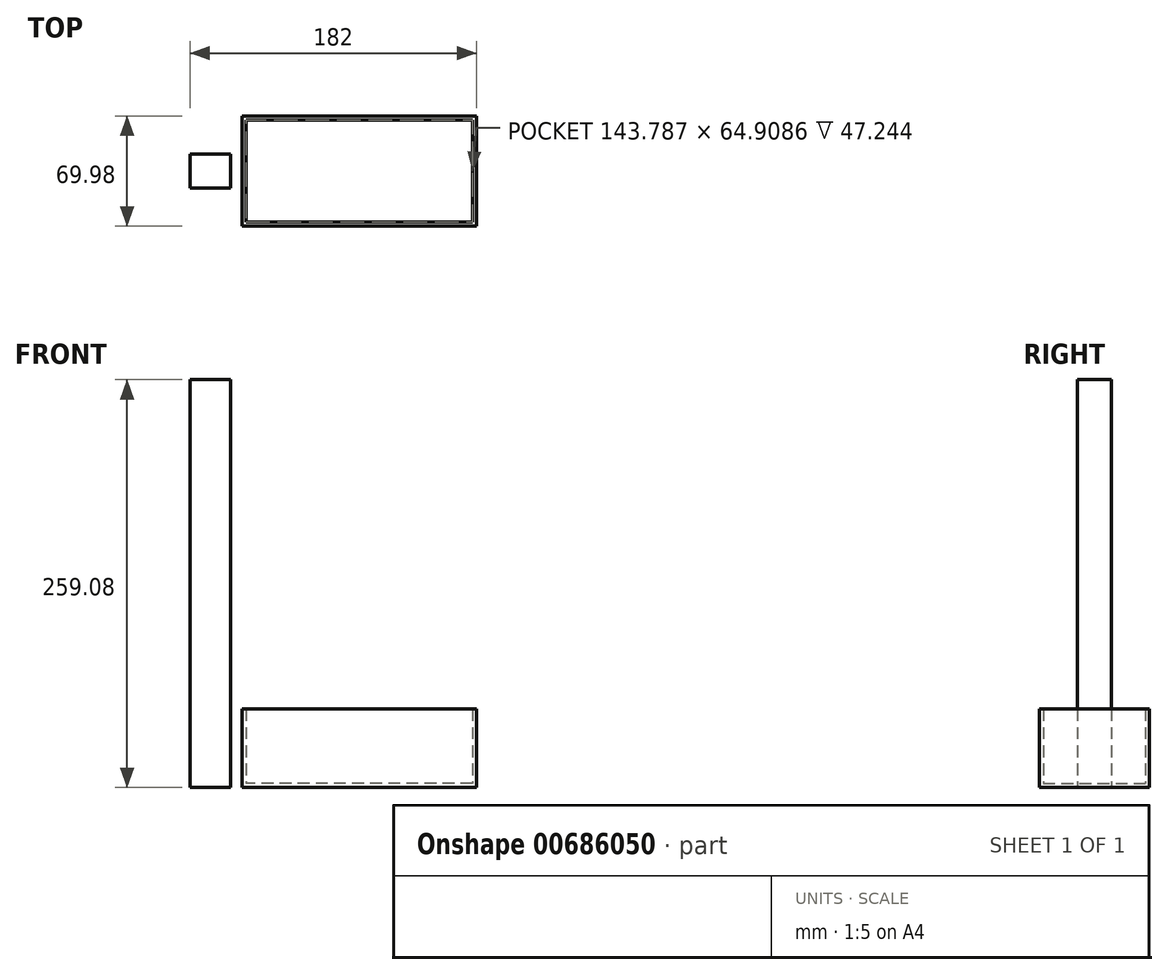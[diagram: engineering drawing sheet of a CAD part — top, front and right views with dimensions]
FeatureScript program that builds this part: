
annotation { "Feature Type Name" : "Feature", "Feature Type Description" : "" }
export const myFeature = defineFeature(function(context is Context, id is Id, definition is map)
    precondition{}
    {
        {
            var Q0;
            Q0=qCreatedBy(makeId("Top.planeOp"),FACE);
            var sketch = newSketch(context, id + "F0", { "sketchPlane" : qUnion([Q0])});
            skLineSegment(sketch, "E0.bottom", {"start": v(74.43, -35) * mm, "end": v(-74.43, -35) * mm});
            skLineSegment(sketch, "E0.top", {"start": v(74.43, 35) * mm, "end": v(-74.43, 35) * mm});
            skLineSegment(sketch, "E0.left", {"start": v(74.43, -35) * mm, "end": v(74.43, 35) * mm});
            skLineSegment(sketch, "E0.right", {"start": v(-74.43, -35) * mm, "end": v(-74.43, 35) * mm});
            skPoint(sketch, "E0.middle", {"position": v(0, 0) * mm});
            skSolve(sketch);
        }
        {
            var Q0;
            Q0=makeQuery(id+"F0.imprint","IMPRINT",FACE,{"disambiguationData":[TD([[makeQuery(id+"F0.imprint","IMPRINT",EDGE,{"derivedFrom":sQuery(id+"F0.wireOp",EDGE,"E0.bottom")}),-1.0]])]});
            extrude(context, id + "F1", {"entities" : qUnion([Q0]), "depth" : 49.78 * mm, "offsetDistance" : 25.4 * mm});
        }
        {
            var Q0;
            Q0=makeQuery(id+"F1.opExtrude","CAP_FACE",FACE,{"disambiguationData":[OSD([sQuery(id+"F0.wireOp",EDGE,"E0.bottom"),sQuery(id+"F0.wireOp",EDGE,"E0.top"),sQuery(id+"F0.wireOp",EDGE,"E0.left"),sQuery(id+"F0.wireOp",EDGE,"E0.right")])],"isStart":false});
            shell(context, id + "F2", {"entities" : qUnion([Q0]), "thickness" : 2.54 * mm});
        }
        {
            var Q0;
            Q0=qCreatedBy(makeId("Top.planeOp"),FACE);
            var sketch = newSketch(context, id + "F3", { "sketchPlane" : qUnion([Q0])});
            skLineSegment(sketch, "E1.bottom", {"start": v(-81.7, -10.75) * mm, "end": v(-107.57, -10.75) * mm});
            skLineSegment(sketch, "E1.top", {"start": v(-81.7, 10.75) * mm, "end": v(-107.57, 10.75) * mm});
            skLineSegment(sketch, "E1.left", {"start": v(-81.7, -10.75) * mm, "end": v(-81.7, 10.75) * mm});
            skLineSegment(sketch, "E1.right", {"start": v(-107.57, -10.75) * mm, "end": v(-107.57, 10.75) * mm});
            skPoint(sketch, "E1.middle", {"position": v(-94.64, 0) * mm});
            skSolve(sketch);
        }
        {
            var Q0;
            Q0=makeQuery(id+"F3.imprint","IMPRINT",FACE,{"disambiguationData":[TD([[makeQuery(id+"F3.imprint","IMPRINT",EDGE,{"derivedFrom":sQuery(id+"F3.wireOp",EDGE,"E1.bottom")}),-1.0]])]});
            extrude(context, id + "F4", {"entities" : qUnion([Q0]), "depth" : 259.08 * mm, "offsetDistance" : 25.4 * mm});
        }
    });
